# Revit family: EKF_EE_ПанельМонтажнаяЩРМ_PROxima
name_source: partatom
category: Электрооборудование
units: mm (PartAtom-declared; Revit-internal decimal feet)

## family parameters
Всегда вертикально = Нет
На основе рабочей плоскости = Да
Общий = Да
При загрузке вырезать с полостями = Нет
Размер круглого соединителя = Использовать диаметр
Тип детали = Силовой щит
Точка расчета площади = Нет

## types (12) — shared parameters
ADSK_Единица измерения = шт.
ADSK_Завод-изготовитель = EKF
ADSK_Количество = 1
ADSK_Марка = Панель монтажная
ADSK_Материал = RAL 7035_Сталь
ADSK_Обозначение = Панель монтажная
ADSK_Размер_Глубина = 32.5 мм
D = 10 мм
Изготовитель = EKF
Отступ = 20 мм
Серия номенклатуры = PROxima
Степень защиты IP = -
ТВ = EKF_2
Тип установки = -
zero-valued in all types: ADSK_Масса, Отметка по умолчанию

## per-type parameters (varying)
| type | ADSK_Код изделия | ADSK_Наименование | ADSK_Размер_Высота | ADSK_Размер_Ширина | t | КолОтв | Тип |
| Панель монтажная (1560x545х2) (ЩРНМ-8) EKF PROxima | pm-1560x540s | Панель монтажная (1560x545х2) (ЩРНМ-8) EKF PROxima | 1560 мм | 545 мм | 2.5 мм | 3 | 126 мм |
| Панель монтажная (1560x745х2) (ЩРНМ-8L) EKF PROxima | pm-1560x740s | Панель монтажная (1560x745х2) (ЩРНМ-8L) EKF PROxima | 1560 мм | 745 мм | 2.5 мм | 3 | 127 мм |
| Панель монтажная (1760x545х2) (ЩРНМ-9) EKF PROxima | pm-1760x540s | Панель монтажная (1760x545х2) (ЩРНМ-9) EKF PROxima | 1760 мм | 545 мм | 2.5 мм | 3 | 128 мм |
| Панель монтажная (1760x745х2) (ЩРНМ-9L) EKF PROxima | pm-1760x740s | Панель монтажная (1760x745х2) (ЩРНМ-9L) EKF PROxima | 1760 мм | 745 мм | 2.5 мм | 3 | 129 мм |
| Панель монтажная (300x545мм) (ЩРНМ-8, ЩРНМ-9) EKF PROxima | pm-300x545 | Панель монтажная (300x545мм) (ЩРНМ-8 ЩРНМ-9) EKF PROxima | 300 мм | 545 мм | 1.5 мм | 2 | 130 мм |
| Панель монтажная (300x545х2) (ЩРНМ-8, ЩРНМ-9) EKF PROxima | pm-300x540s | Панель монтажная (300x545х2) (ЩРНМ-8 ЩРНМ-9) EKF PROxima | 300 мм | 545 мм | 2 мм | 2 | 131 мм |
| Панель монтажная (300x745мм) (ЩРНМ-8L, ЩРНМ-9L) EKF PROxima | pm-300x745 | Панель монтажная (300x745мм) (ЩРНМ-8L ЩРНМ-9L) EKF PROxima | 300 мм | 745 мм | 1.5 мм | 2 | 132 мм |
| Панель монтажная (300x745х2) (ЩРНМ-8L, ЩРНМ-9L) EKF PROxima | pm-300x740s | Панель монтажная (300x745х2) (ЩРНМ-8L ЩРНМ-9L) EKF PROxima | 300 мм | 745 мм | 2 мм | 2 | 133 мм |
| Панель монтажная (500x545мм) (ЩРНМ-8, ЩРНМ-9) EKF PROxima | pm-500x545 | Панель монтажная (500x545мм) (ЩРНМ-8 ЩРНМ-9) EKF PROxima | 500 мм | 545 мм | 1.5 мм | 2 | 134 мм |
| Панель монтажная (500x545х2) (ЩРНМ-8, ЩРНМ-9) EKF PROxima | pm-500x540s | Панель монтажная (500x545х2) (ЩРНМ-8 ЩРНМ-9) EKF PROxima | 500 мм | 545 мм | 2 мм | 2 | 135 мм |
| Панель монтажная (500x745мм) (ЩРНМ-8L, ЩРНМ-9L) EKF PROxima | pm-500x745 | Панель монтажная (500x745мм) (ЩРНМ-8L ЩРНМ-9L) EKF PROxima | 500 мм | 745 мм | 1.5 мм | 2 | 136 мм |
| Панель монтажная (500x745х2) (ЩРНМ-8L, ЩРНМ-9L) EKF PROxima | pm-500x740s | Панель монтажная (500x745х2) (ЩРНМ-8L ЩРНМ-9L) EKF PROxima | 500 мм | 745 мм | 2 мм | 2 | 137 мм |
